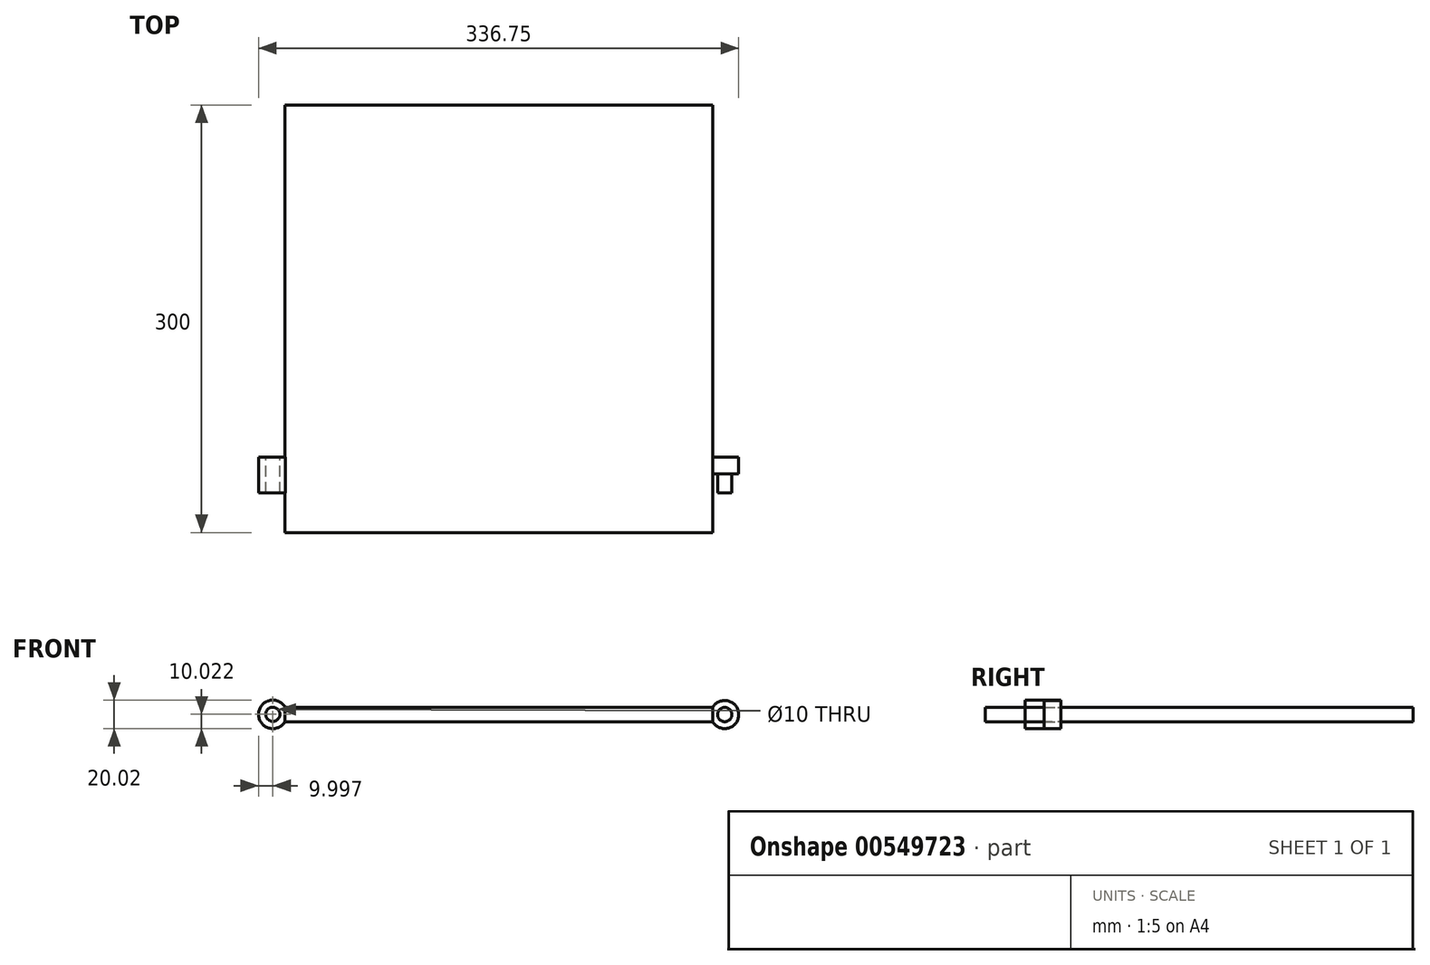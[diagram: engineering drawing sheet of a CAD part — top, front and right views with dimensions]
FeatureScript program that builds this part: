
annotation { "Feature Type Name" : "Feature", "Feature Type Description" : "" }
export const myFeature = defineFeature(function(context is Context, id is Id, definition is map)
    precondition{}
    {
        {
            var Q0;
            Q0=qCreatedBy(makeId("Top.planeOp"),FACE);
            var sketch = newSketch(context, id + "F0", { "sketchPlane" : qUnion([Q0])});
            skLineSegment(sketch, "E0.bottom", {"start": v(-243.32, 247.14) * mm, "end": v(56.68, 247.14) * mm});
            skLineSegment(sketch, "E0.top", {"start": v(-243.32, -52.86) * mm, "end": v(56.68, -52.86) * mm});
            skLineSegment(sketch, "E0.left", {"start": v(-243.32, 247.14) * mm, "end": v(-243.32, -52.86) * mm});
            skLineSegment(sketch, "E0.right", {"start": v(56.68, 247.14) * mm, "end": v(56.68, -52.86) * mm});
            skSolve(sketch);
        }
        {
            var Q0;
            Q0 = qSketchRegion(id + "F0", true);
            extrude(context, id + "F1", {"entities" : qUnion([Q0]), "depth" : 10 * mm, "offsetDistance" : 25 * mm});
        }
        {
            var Q0;
            Q0=qCreatedBy(makeId("Front.planeOp"),FACE);
            var sketch = newSketch(context, id + "F2", { "sketchPlane" : qUnion([Q0])});
            skCircle(sketch, "E1", {"center": v(-251.92, 5.2) * mm, "radius": 10 * mm});
            skCircle(sketch, "E2.0", {"center": v(-251.92, 5.2) * mm, "radius": 5 * mm});
            skCircle(sketch, "E3", {"center": v(65, 5) * mm, "radius": 9.83 * mm});
            skSolve(sketch);
        }
        {
            var Q0;
            Q0 = qSketchRegion(id + "F2", true);
            extrude(context, id + "F3", {"entities" : qUnion([Q0]), "operationType" : NewBodyOperationType.ADD, "depth" : 25 * mm, "offsetDistance" : 25 * mm});
        }
        {
            var Q0;
            Q0=makeQuery(id+"F3.opExtrude","CAP_FACE",FACE,{"disambiguationData":[OSD([sQuery(id+"F2.wireOp",EDGE,"E3")])],"isStart":false});
            var sketch = newSketch(context, id + "F4", { "sketchPlane" : qUnion([Q0])});
            skCircle(sketch, "E4", {"center": v(65, 5) * mm, "radius": 5 * mm});
            skSolve(sketch);
        }
        {
            var Q0;
            Q0=makeQuery(id+"F4.imprint","IMPRINT",FACE,{"disambiguationData":[TD([[makeQuery(id+"F4.imprint","IMPRINT",EDGE,{"derivedFrom":sQuery(id+"F4.wireOp",EDGE,"E4")}),-1.0]])]});
            extrude(context, id + "F5", {"entities" : qUnion([Q0]), "operationType" : NewBodyOperationType.REMOVE, "oppositeDirection" : true, "depth" : 13.4 * mm, "offsetDistance" : 25 * mm});
        }
    });
